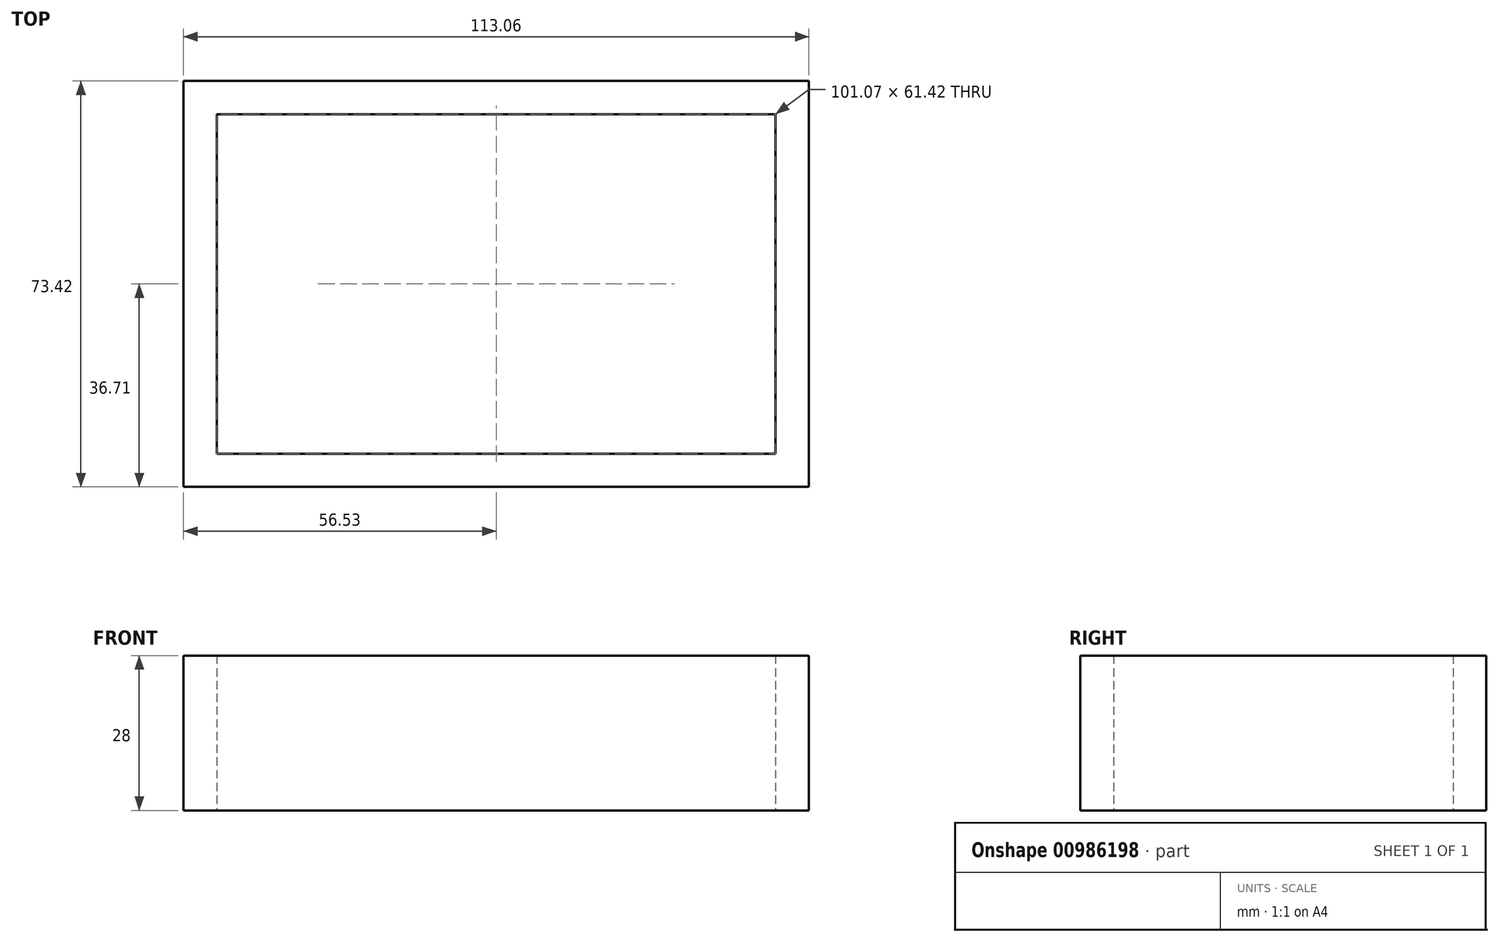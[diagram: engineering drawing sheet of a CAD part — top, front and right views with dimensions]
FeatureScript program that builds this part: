
annotation { "Feature Type Name" : "Feature", "Feature Type Description" : "" }
export const myFeature = defineFeature(function(context is Context, id is Id, definition is map)
    precondition{}
    {
        {
            var Q0;
            Q0=qCreatedBy(makeId("Top.planeOp"),FACE);
            var sketch = newSketch(context, id + "F0", { "sketchPlane" : qUnion([Q0])});
            skLineSegment(sketch, "E0.bottom", {"start": v(-50.53, 30.7) * mm, "end": v(50.53, 30.7) * mm});
            skLineSegment(sketch, "E0.top", {"start": v(-50.53, -30.7) * mm, "end": v(50.53, -30.7) * mm});
            skLineSegment(sketch, "E0.left", {"start": v(-50.53, 30.7) * mm, "end": v(-50.53, -30.7) * mm});
            skLineSegment(sketch, "E0.right", {"start": v(50.53, 30.7) * mm, "end": v(50.53, -30.7) * mm});
            skPoint(sketch, "E0.middle", {"position": v(0, 0) * mm});
            skLineSegment(sketch, "E1.0", {"start": v(-56.53, 36.7) * mm, "end": v(56.53, 36.7) * mm});
            skLineSegment(sketch, "E1.1", {"start": v(-56.53, 36.7) * mm, "end": v(-56.53, -36.7) * mm});
            skLineSegment(sketch, "E1.2", {"start": v(-56.53, -36.7) * mm, "end": v(56.53, -36.7) * mm});
            skLineSegment(sketch, "E1.3", {"start": v(56.53, 36.7) * mm, "end": v(56.53, -36.7) * mm});
            skLineSegment(sketch, "E2.bottom", {"start": v(36, -19.06) * mm, "end": v(-36, -19.06) * mm, "construction": true});
            skLineSegment(sketch, "E2.top", {"start": v(36, 19.06) * mm, "end": v(-36, 19.06) * mm, "construction": true});
            skLineSegment(sketch, "E2.left", {"start": v(36, -19.06) * mm, "end": v(36, 19.06) * mm, "construction": true});
            skLineSegment(sketch, "E2.right", {"start": v(-36, -19.06) * mm, "end": v(-36, 19.06) * mm, "construction": true});
            skCircle(sketch, "E3", {"center": v(-36, 19.06) * mm, "radius": 5.42 * mm});
            skCircle(sketch, "E4", {"center": v(36, 19.06) * mm, "radius": 5.42 * mm});
            skCircle(sketch, "E5", {"center": v(36, -19.06) * mm, "radius": 5.42 * mm});
            skCircle(sketch, "E6", {"center": v(-36, -19.06) * mm, "radius": 5.42 * mm});
            skSolve(sketch);
        }
        {
            var Q0;
            Q0=makeQuery(id+"F0.imprint","IMPRINT",FACE,{"disambiguationData":[TD([[makeQuery(id+"F0.imprint","IMPRINT",EDGE,{"derivedFrom":sQuery(id+"F0.wireOp",EDGE,"E0.bottom")}),1.0]])]});
            extrude(context, id + "F1", {"entities" : qUnion([Q0]), "depth" : 28 * mm, "offsetDistance" : 25.4 * mm});
        }
    });
